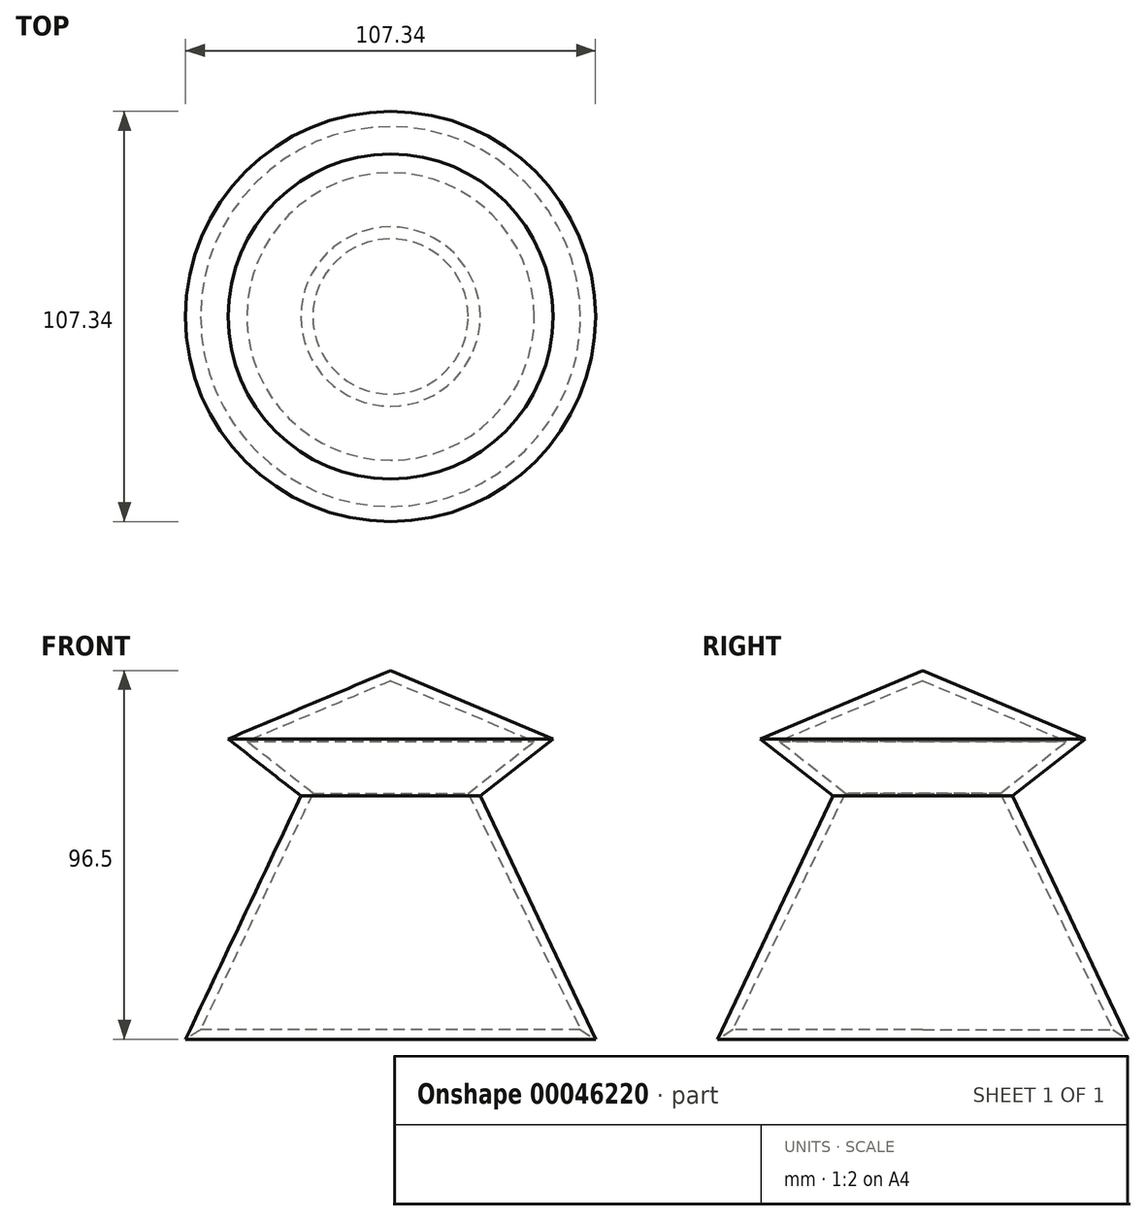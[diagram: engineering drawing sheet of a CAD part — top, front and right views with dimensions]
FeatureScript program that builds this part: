
annotation { "Feature Type Name" : "Feature", "Feature Type Description" : "" }
export const myFeature = defineFeature(function(context is Context, id is Id, definition is map)
    precondition{}
    {
        {
            var Q0;
            Q0=qCreatedBy(makeId("Front.planeOp"),FACE);
            var sketch = newSketch(context, id + "F0", { "sketchPlane" : qUnion([Q0])});
            skLineSegment(sketch, "E0", {"start": v(0, 0) * mm, "end": v(0, 62.62) * mm});
            skLineSegment(sketch, "E1", {"start": v(0, 62.62) * mm, "end": v(-42.53, 44.73) * mm});
            skLineSegment(sketch, "E2", {"start": v(-42.53, 44.73) * mm, "end": v(-23.46, 29.77) * mm});
            skLineSegment(sketch, "E3", {"start": v(-23.46, 29.77) * mm, "end": v(-53.67, -33.88) * mm});
            skLineSegment(sketch, "E4", {"start": v(-53.67, -33.88) * mm, "end": v(0, 0) * mm});
            skSolve(sketch);
        }
        {
            var Q0;
            Q0=makeQuery(id+"F0.imprint","IMPRINT",FACE,{"disambiguationData":[TD([[makeQuery(id+"F0.imprint","IMPRINT",EDGE,{"derivedFrom":sQuery(id+"F0.wireOp",EDGE,"E0")}),1.0]])]});
            var Q1;
            Q1=sQuery(id+"F0.wireOp",EDGE,"E0");
            revolve(context, id + "F1", {"entities" : qUnion([Q0]), "axis" : qUnion([Q1]), "revolveType" : RevolveType.FULL});
        }
        {
            var Q0;
            Q0=makeQuery(id+"F1.opRevolve","SWEPT_FACE",FACE,{"disambiguationData":[OSD([sQuery(id+"F0.wireOp",EDGE,"E4")])]});
            shell(context, id + "F2", {"entities" : qUnion([Q0]), "thickness" : 2.5 * mm});
        }
    });
